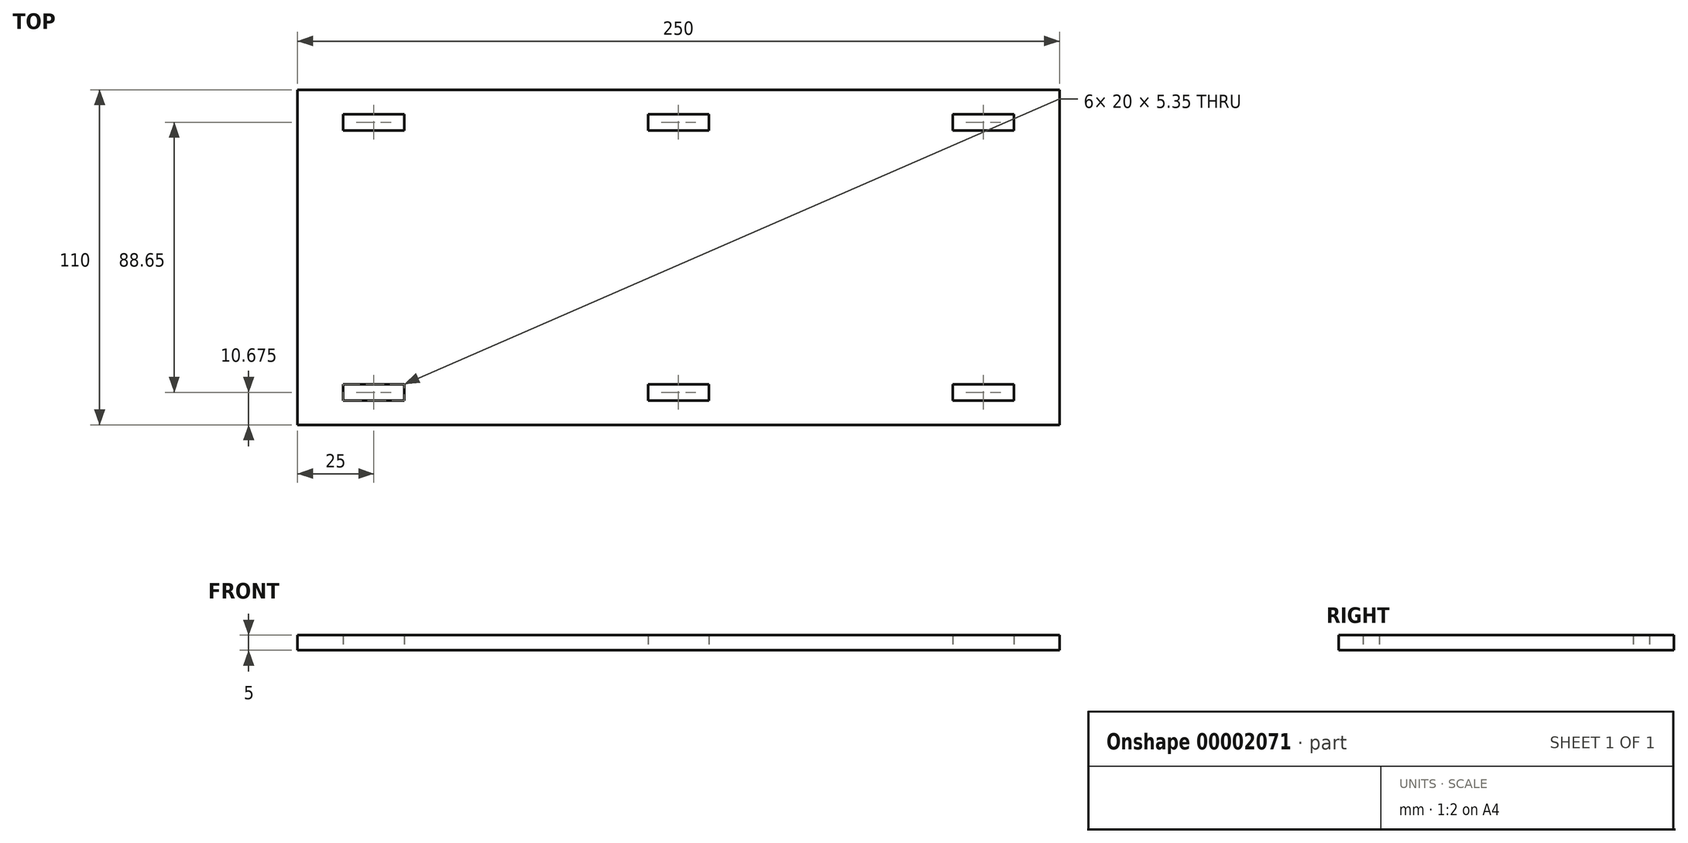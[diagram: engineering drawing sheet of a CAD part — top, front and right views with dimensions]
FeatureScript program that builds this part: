
annotation { "Feature Type Name" : "Feature", "Feature Type Description" : "" }
export const myFeature = defineFeature(function(context is Context, id is Id, definition is map)
    precondition{}
    {
        {
            var Q0;
            Q0=qCreatedBy(makeId("Top.planeOp"),FACE);
            var sketch = newSketch(context, id + "F0", { "sketchPlane" : qUnion([Q0])});
            skLineSegment(sketch, "E0.bottom", {"start": v(0, 0) * mm, "end": v(0, 0) * mm});
            skLineSegment(sketch, "E0.top", {"start": v(0, 53.66) * mm, "end": v(0, 53.66) * mm});
            skLineSegment(sketch, "E1.top", {"start": v(0, -56.34) * mm, "end": v(0, -56.34) * mm});
            skLineSegment(sketch, "E2.bottom", {"start": v(0, 53.66) * mm, "end": v(250, 53.66) * mm});
            skLineSegment(sketch, "E2.top", {"start": v(-3.27, -56.34) * mm, "end": v(250, -56.34) * mm});
            skLineSegment(sketch, "E3", {"start": v(0, 53.66) * mm, "end": v(0, 44.52) * mm});
            skLineSegment(sketch, "E4", {"start": v(0, -47.2) * mm, "end": v(0, -56.34) * mm});
            skLineSegment(sketch, "E5", {"start": v(0, -47.2) * mm, "end": v(0, 44.52) * mm});
            skLineSegment(sketch, "E6", {"start": v(250, 44.52) * mm, "end": v(250, -47.2) * mm});
            skLineSegment(sketch, "E7", {"start": v(250, -47.2) * mm, "end": v(250, -56.34) * mm});
            skLineSegment(sketch, "E8", {"start": v(250, 44.52) * mm, "end": v(250, 53.66) * mm});
            skLineSegment(sketch, "E9", {"start": v(15, 40.3) * mm, "end": v(15, 45.66) * mm});
            skLineSegment(sketch, "E10", {"start": v(35, 40.3) * mm, "end": v(35, 45.66) * mm});
            skLineSegment(sketch, "E11", {"start": v(15, -43) * mm, "end": v(15, -48.34) * mm});
            skLineSegment(sketch, "E12", {"start": v(35, -43) * mm, "end": v(35, -48.34) * mm});
            skLineSegment(sketch, "E13", {"start": v(215, -48.34) * mm, "end": v(215, -43) * mm});
            skLineSegment(sketch, "E14", {"start": v(235, -48.34) * mm, "end": v(235, -43) * mm});
            skLineSegment(sketch, "E15", {"start": v(235, 40.3) * mm, "end": v(235, 45.66) * mm});
            skLineSegment(sketch, "E16", {"start": v(215, 40.3) * mm, "end": v(215, 45.66) * mm});
            skLineSegment(sketch, "E17", {"start": v(15, 45.66) * mm, "end": v(35, 45.66) * mm});
            skLineSegment(sketch, "E18", {"start": v(35, 40.3) * mm, "end": v(15, 40.3) * mm});
            skLineSegment(sketch, "E19", {"start": v(215, 40.3) * mm, "end": v(235, 40.3) * mm});
            skLineSegment(sketch, "E20", {"start": v(235, 45.66) * mm, "end": v(215, 45.66) * mm});
            skLineSegment(sketch, "E21", {"start": v(15, -43) * mm, "end": v(35, -43) * mm});
            skLineSegment(sketch, "E22", {"start": v(35, -48.34) * mm, "end": v(15, -48.34) * mm});
            skLineSegment(sketch, "E23", {"start": v(215, -48.34) * mm, "end": v(235, -48.34) * mm});
            skLineSegment(sketch, "E24", {"start": v(235, -43) * mm, "end": v(215, -43) * mm});
            skLineSegment(sketch, "E25", {"start": v(115, 40.3) * mm, "end": v(135, 40.3) * mm});
            skLineSegment(sketch, "E26", {"start": v(135, 40.3) * mm, "end": v(135, 45.66) * mm});
            skLineSegment(sketch, "E27", {"start": v(135, 45.66) * mm, "end": v(115, 45.66) * mm});
            skLineSegment(sketch, "E28", {"start": v(115, 45.66) * mm, "end": v(115, 40.3) * mm});
            skLineSegment(sketch, "E29", {"start": v(125, 53.66) * mm, "end": v(125, 45.66) * mm, "construction": true});
            skLineSegment(sketch, "E30", {"start": v(115, -43) * mm, "end": v(135, -43) * mm});
            skLineSegment(sketch, "E31", {"start": v(135, -43) * mm, "end": v(135, -48.34) * mm});
            skLineSegment(sketch, "E32", {"start": v(135, -48.34) * mm, "end": v(115, -48.34) * mm});
            skLineSegment(sketch, "E33", {"start": v(115, -48.34) * mm, "end": v(115, -43) * mm});
            skLineSegment(sketch, "E34", {"start": v(225, 40.3) * mm, "end": v(225, -43) * mm, "construction": true});
            skLineSegment(sketch, "E35", {"start": v(25, 40.3) * mm, "end": v(25, -43) * mm, "construction": true});
            skLineSegment(sketch, "E36", {"start": v(35, 40.3) * mm, "end": v(115, 40.3) * mm, "construction": true});
            skLineSegment(sketch, "E37", {"start": v(135, 40.3) * mm, "end": v(215, 40.3) * mm, "construction": true});
            skSolve(sketch);
        }
        {
            var Q0;
            Q0=makeQuery(id+"F0.imprint","IMPRINT",FACE,{"disambiguationData":[TD([[makeQuery(id+"F0.imprint","IMPRINT",EDGE,{"derivedFrom":sQuery(id+"F0.wireOp",EDGE,"E2.bottom")}),-1.0]])]});
            extrude(context, id + "F1", {"entities" : qUnion([Q0]), "depth" : 5 * mm});
        }
    });
